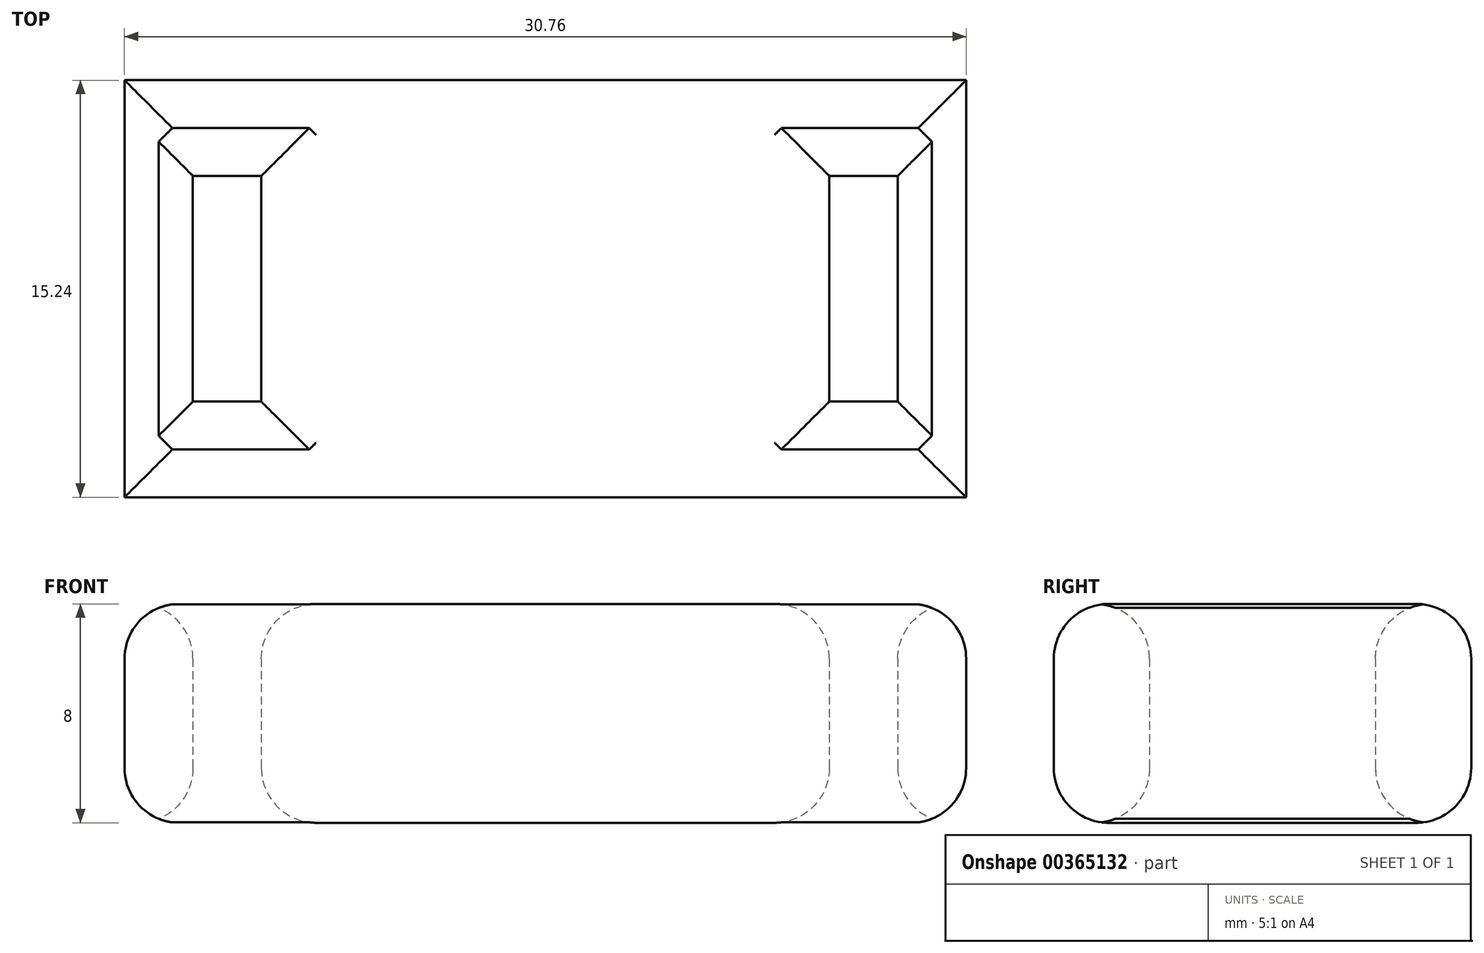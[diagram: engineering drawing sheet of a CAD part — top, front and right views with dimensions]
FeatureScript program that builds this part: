
annotation { "Feature Type Name" : "Feature", "Feature Type Description" : "" }
export const myFeature = defineFeature(function(context is Context, id is Id, definition is map)
    precondition{}
    {
        {
            var Q0;
            Q0=qCreatedBy(makeId("Top.planeOp"),FACE);
            var sketch = newSketch(context, id + "F0", { "sketchPlane" : qUnion([Q0])});
            skLineSegment(sketch, "E0.bottom", {"start": v(-15.38, 7.63) * mm, "end": v(15.38, 7.63) * mm});
            skLineSegment(sketch, "E0.top", {"start": v(-15.38, -7.63) * mm, "end": v(15.38, -7.63) * mm});
            skLineSegment(sketch, "E0.left", {"start": v(-15.38, 7.63) * mm, "end": v(-15.38, -7.63) * mm});
            skLineSegment(sketch, "E0.right", {"start": v(15.38, 7.63) * mm, "end": v(15.38, -7.63) * mm});
            skPoint(sketch, "E0.middle", {"position": v(0, 0) * mm});
            skLineSegment(sketch, "E1.bottom", {"start": v(10.37, 4.13) * mm, "end": v(12.88, 4.13) * mm});
            skLineSegment(sketch, "E1.top", {"start": v(10.37, -4.12) * mm, "end": v(12.88, -4.12) * mm});
            skLineSegment(sketch, "E1.left", {"start": v(10.37, 4.13) * mm, "end": v(10.37, -4.12) * mm});
            skLineSegment(sketch, "E1.right", {"start": v(12.88, 4.13) * mm, "end": v(12.88, -4.12) * mm});
            skPoint(sketch, "E1.middle", {"position": v(11.62, 0) * mm});
            skLineSegment(sketch, "E2.MirrorCS", {"start": v(-10.37, 4.13) * mm, "end": v(-10.37, -4.12) * mm});
            skLineSegment(sketch, "E3.MirrorCS", {"start": v(-10.37, 4.12) * mm, "end": v(-12.88, 4.12) * mm});
            skLineSegment(sketch, "E4.MirrorCS", {"start": v(-12.88, 4.13) * mm, "end": v(-12.88, -4.12) * mm});
            skLineSegment(sketch, "E5.MirrorCS", {"start": v(-10.37, -4.13) * mm, "end": v(-12.88, -4.13) * mm});
            skSolve(sketch);
        }
        {
            var Q0;
            Q0=makeQuery(id+"F0.imprint","IMPRINT",FACE,{"disambiguationData":[TD([[makeQuery(id+"F0.imprint","IMPRINT",EDGE,{"derivedFrom":sQuery(id+"F0.wireOp",EDGE,"E0.bottom")}),-1.0]])]});
            extrude(context, id + "F1", {"entities" : qUnion([Q0]), "depth" : 8 * mm});
        }
        {
            var Q0;
            Q0=makeQuery(id+"F1.opExtrude","CAP_FACE",FACE,{"disambiguationData":[OSD([sQuery(id+"F0.wireOp",EDGE,"E0.bottom"),sQuery(id+"F0.wireOp",EDGE,"E0.top"),sQuery(id+"F0.wireOp",EDGE,"E0.left"),sQuery(id+"F0.wireOp",EDGE,"E0.right"),sQuery(id+"F0.wireOp",EDGE,"E1.bottom"),sQuery(id+"F0.wireOp",EDGE,"E1.top"),sQuery(id+"F0.wireOp",EDGE,"E1.left"),sQuery(id+"F0.wireOp",EDGE,"E1.right"),sQuery(id+"F0.wireOp",EDGE,"E2.MirrorCS"),sQuery(id+"F0.wireOp",EDGE,"E3.MirrorCS"),sQuery(id+"F0.wireOp",EDGE,"E4.MirrorCS"),sQuery(id+"F0.wireOp",EDGE,"E5.MirrorCS")])],"isStart":false});
            var Q1;
            Q1=makeQuery(id+"F1.opExtrude","CAP_FACE",FACE,{"disambiguationData":[OSD([sQuery(id+"F0.wireOp",EDGE,"E0.bottom"),sQuery(id+"F0.wireOp",EDGE,"E0.top"),sQuery(id+"F0.wireOp",EDGE,"E0.left"),sQuery(id+"F0.wireOp",EDGE,"E0.right"),sQuery(id+"F0.wireOp",EDGE,"E1.bottom"),sQuery(id+"F0.wireOp",EDGE,"E1.top"),sQuery(id+"F0.wireOp",EDGE,"E1.left"),sQuery(id+"F0.wireOp",EDGE,"E1.right"),sQuery(id+"F0.wireOp",EDGE,"E2.MirrorCS"),sQuery(id+"F0.wireOp",EDGE,"E3.MirrorCS"),sQuery(id+"F0.wireOp",EDGE,"E4.MirrorCS"),sQuery(id+"F0.wireOp",EDGE,"E5.MirrorCS")])],"isStart":true});
            fillet(context, id + "F2", {"entities" : qUnion([Q0, Q1]), "radius" : 2 * mm, "tangentPropagation" : true, "allowEdgeOverflow" : false});
        }
    });
